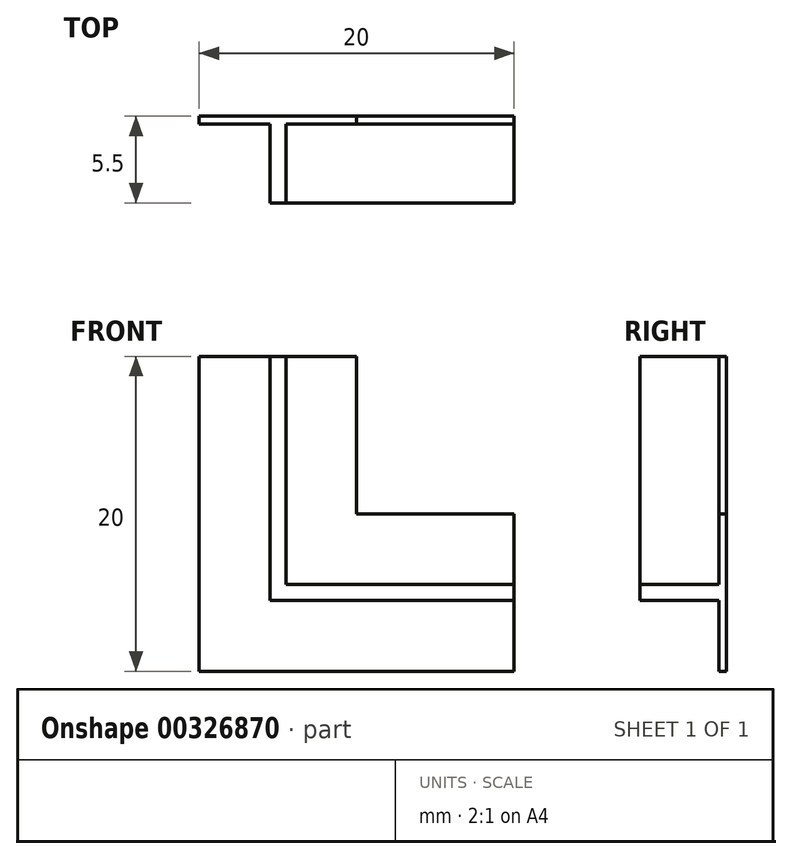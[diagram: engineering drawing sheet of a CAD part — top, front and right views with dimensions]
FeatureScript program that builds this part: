
annotation { "Feature Type Name" : "Feature", "Feature Type Description" : "" }
export const myFeature = defineFeature(function(context is Context, id is Id, definition is map)
    precondition{}
    {
        {
            var Q0;
            Q0=qCreatedBy(makeId("Front.planeOp"),FACE);
            var sketch = newSketch(context, id + "F0", { "sketchPlane" : qUnion([Q0])});
            skLineSegment(sketch, "E0.bottom", {"start": v(-68, -28.7) * mm, "end": v(-48, -28.7) * mm});
            skLineSegment(sketch, "E0.left", {"start": v(-68, -28.7) * mm, "end": v(-68, -8.7) * mm});
            skLineSegment(sketch, "E1.0", {"start": v(-62.5, -23.2) * mm, "end": v(-48, -23.2) * mm});
            skLineSegment(sketch, "E1.1", {"start": v(-62.5, -23.2) * mm, "end": v(-62.5, -8.7) * mm});
            skLineSegment(sketch, "E2", {"start": v(-48, -23.2) * mm, "end": v(-48, -28.7) * mm});
            skLineSegment(sketch, "E3", {"start": v(-68, -8.7) * mm, "end": v(-62.5, -8.7) * mm});
            skLineSegment(sketch, "E4.0", {"start": v(-58, -18.7) * mm, "end": v(-58, -8.7) * mm});
            skLineSegment(sketch, "E4.1", {"start": v(-58, -18.7) * mm, "end": v(-48, -18.7) * mm});
            skLineSegment(sketch, "E5", {"start": v(-62.5, -8.7) * mm, "end": v(-58, -8.7) * mm});
            skLineSegment(sketch, "E6", {"start": v(-48, -23.2) * mm, "end": v(-48, -18.7) * mm});
            skLineSegment(sketch, "E7", {"start": v(-63.5, -24.2) * mm, "end": v(-48, -24.2) * mm});
            skLineSegment(sketch, "E8", {"start": v(-63.5, -8.7) * mm, "end": v(-63.5, -24.2) * mm});
            skSolve(sketch);
        }
        {
            var Q0;
            {var subQ1=sQuery(id+"F0.wireOp",EDGE,"E1.0");Q0=makeQuery(id+"F0.imprint","IMPRINT",FACE,{"disambiguationData":[TD([[makeQuery(id+"F0.imprint","IMPRINT",EDGE,{"derivedFrom":subQ1}),-1.0]])]});}
            extrude(context, id + "F1", {"entities" : qUnion([Q0]), "depth" : 5 * mm});
        }
        {
            var Q0;
            {var subQ5=sQuery(id+"F0.wireOp",EDGE,"E0.bottom");Q0=makeQuery(id+"F0.imprint","IMPRINT",FACE,{"disambiguationData":[TD([[makeQuery(id+"F0.imprint","IMPRINT",EDGE,{"derivedFrom":subQ5}),1.0]])]});}
            var Q1;
            {var subQ1=sQuery(id+"F0.wireOp",EDGE,"E1.0");Q1=makeQuery(id+"F0.imprint","IMPRINT",FACE,{"disambiguationData":[TD([[makeQuery(id+"F0.imprint","IMPRINT",EDGE,{"derivedFrom":subQ1}),-1.0]])]});}
            var Q2;
            Q2=makeQuery(id+"F0.imprint","IMPRINT",FACE,{"disambiguationData":[TD([[makeQuery(id+"F0.imprint","IMPRINT",EDGE,{"derivedFrom":sQuery(id+"F0.wireOp",EDGE,"E1.0")}),1.0]])]});
            extrude(context, id + "F2", {"entities" : qUnion([Q0, Q1, Q2]), "operationType" : NewBodyOperationType.ADD, "depth" : -0.5 * mm});
        }
    });
